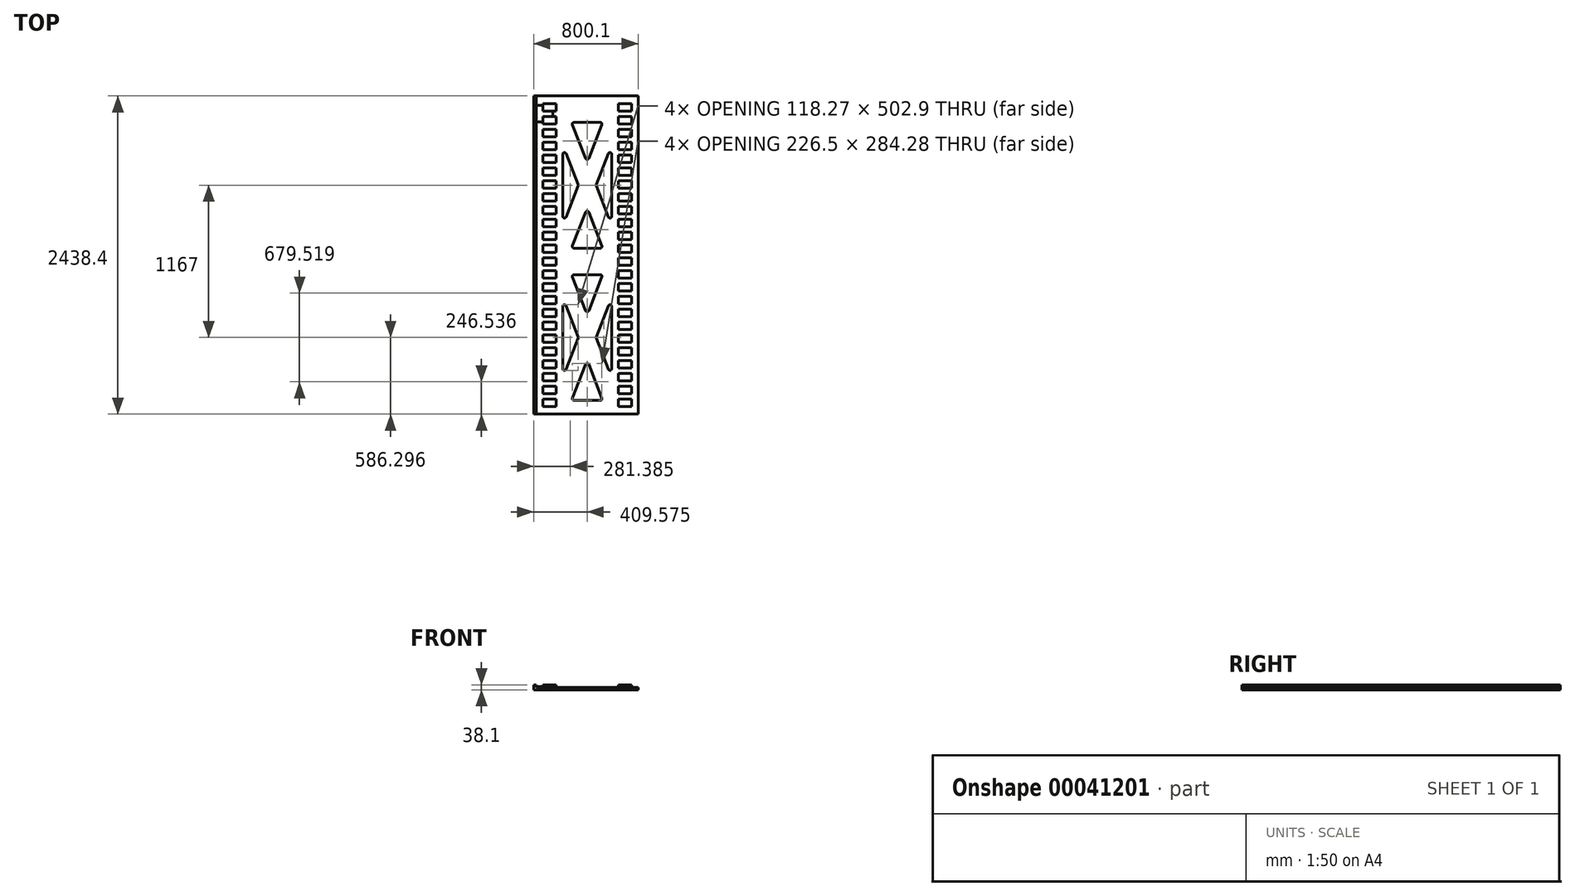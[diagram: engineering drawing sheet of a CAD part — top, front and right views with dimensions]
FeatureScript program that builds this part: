
annotation { "Feature Type Name" : "Feature", "Feature Type Description" : "" }
export const myFeature = defineFeature(function(context is Context, id is Id, definition is map)
    precondition{}
    {
        {
            var Q0;
            Q0=qCreatedBy(makeId("Front.planeOp"),FACE);
            var sketch = newSketch(context, id + "F0", { "sketchPlane" : qUnion([Q0])});
            skLineSegment(sketch, "E0.bottom", {"start": v(0, 0) * mm, "end": v(781.05, 0) * mm});
            skLineSegment(sketch, "E0.top", {"start": v(0, 19.05) * mm, "end": v(781.05, 19.05) * mm});
            skLineSegment(sketch, "E0.left", {"start": v(0, 0) * mm, "end": v(0, 19.05) * mm});
            skLineSegment(sketch, "E0.right", {"start": v(781.05, 0) * mm, "end": v(781.05, 19.05) * mm});
            skSolve(sketch);
        }
        {
            var Q0;
            Q0 = qSketchRegion(id + "F0", true);
            extrude(context, id + "F1", {"entities" : qUnion([Q0]), "depth" : 2438.4 * mm});
        }
        {
            var Q0;
            Q0=makeQuery(id+"F1.opExtrude","SWEPT_FACE",FACE,{"disambiguationData":[OSD([sQuery(id+"F0.wireOp",EDGE,"E0.top")])]});
            var sketch = newSketch(context, id + "F2", { "sketchPlane" : qUnion([Q0])});
            skLineSegment(sketch, "E1.top", {"start": v(50.8, -60.96) * mm, "end": v(152.4, -60.96) * mm});
            skLineSegment(sketch, "E2.top", {"start": v(50.8, -116.71) * mm, "end": v(152.4, -116.71) * mm});
            skLineSegment(sketch, "E2.left", {"start": v(50.8, -60.96) * mm, "end": v(50.8, -116.71) * mm});
            skLineSegment(sketch, "E3", {"start": v(152.4, -60.96) * mm, "end": v(152.4, -116.71) * mm});
            skLineSegment(sketch, "E4.0.1.0", {"start": v(50.8, -159.38) * mm, "end": v(152.4, -159.38) * mm});
            skLineSegment(sketch, "E4.0.1.1", {"start": v(50.8, -215.14) * mm, "end": v(152.4, -215.14) * mm});
            skLineSegment(sketch, "E4.0.1.2", {"start": v(50.8, -159.38) * mm, "end": v(50.8, -215.14) * mm});
            skLineSegment(sketch, "E4.0.1.3", {"start": v(152.4, -159.39) * mm, "end": v(152.4, -215.14) * mm});
            skLineSegment(sketch, "E4.0.2.0", {"start": v(50.8, -257.81) * mm, "end": v(152.4, -257.81) * mm});
            skLineSegment(sketch, "E4.0.2.1", {"start": v(50.8, -313.56) * mm, "end": v(152.4, -313.56) * mm});
            skLineSegment(sketch, "E4.0.2.2", {"start": v(50.8, -257.81) * mm, "end": v(50.8, -313.56) * mm});
            skLineSegment(sketch, "E4.0.2.3", {"start": v(152.4, -257.8) * mm, "end": v(152.4, -313.56) * mm});
            skLineSegment(sketch, "E4.0.3.0", {"start": v(50.8, -356.24) * mm, "end": v(152.4, -356.24) * mm});
            skLineSegment(sketch, "E4.0.3.1", {"start": v(50.8, -411.99) * mm, "end": v(152.4, -411.99) * mm});
            skLineSegment(sketch, "E4.0.3.2", {"start": v(50.8, -356.24) * mm, "end": v(50.8, -411.99) * mm});
            skLineSegment(sketch, "E4.0.3.3", {"start": v(152.4, -356.24) * mm, "end": v(152.4, -411.99) * mm});
            skLineSegment(sketch, "E4.0.4.0", {"start": v(50.8, -454.66) * mm, "end": v(152.4, -454.66) * mm});
            skLineSegment(sketch, "E4.0.4.1", {"start": v(50.8, -510.41) * mm, "end": v(152.4, -510.41) * mm});
            skLineSegment(sketch, "E4.0.4.2", {"start": v(50.8, -454.66) * mm, "end": v(50.8, -510.41) * mm});
            skLineSegment(sketch, "E4.0.4.3", {"start": v(152.4, -454.66) * mm, "end": v(152.4, -510.41) * mm});
            skLineSegment(sketch, "E4.0.5.0", {"start": v(50.8, -553.09) * mm, "end": v(152.4, -553.09) * mm});
            skLineSegment(sketch, "E4.0.5.1", {"start": v(50.8, -608.84) * mm, "end": v(152.4, -608.84) * mm});
            skLineSegment(sketch, "E4.0.5.2", {"start": v(50.8, -553.09) * mm, "end": v(50.8, -608.84) * mm});
            skLineSegment(sketch, "E4.0.5.3", {"start": v(152.4, -553.09) * mm, "end": v(152.4, -608.84) * mm});
            skLineSegment(sketch, "E4.0.6.0", {"start": v(50.8, -651.51) * mm, "end": v(152.4, -651.51) * mm});
            skLineSegment(sketch, "E4.0.6.1", {"start": v(50.8, -707.26) * mm, "end": v(152.4, -707.26) * mm});
            skLineSegment(sketch, "E4.0.6.2", {"start": v(50.8, -651.5) * mm, "end": v(50.8, -707.26) * mm});
            skLineSegment(sketch, "E4.0.6.3", {"start": v(152.4, -651.51) * mm, "end": v(152.4, -707.26) * mm});
            skLineSegment(sketch, "E4.0.7.0", {"start": v(50.8, -749.94) * mm, "end": v(152.4, -749.94) * mm});
            skLineSegment(sketch, "E4.0.7.1", {"start": v(50.8, -805.69) * mm, "end": v(152.4, -805.69) * mm});
            skLineSegment(sketch, "E4.0.7.2", {"start": v(50.8, -749.94) * mm, "end": v(50.8, -805.69) * mm});
            skLineSegment(sketch, "E4.0.7.3", {"start": v(152.4, -749.94) * mm, "end": v(152.4, -805.69) * mm});
            skLineSegment(sketch, "E4.0.8.0", {"start": v(50.8, -848.36) * mm, "end": v(152.4, -848.36) * mm});
            skLineSegment(sketch, "E4.0.8.1", {"start": v(50.8, -904.11) * mm, "end": v(152.4, -904.11) * mm});
            skLineSegment(sketch, "E4.0.8.2", {"start": v(50.8, -848.36) * mm, "end": v(50.8, -904.11) * mm});
            skLineSegment(sketch, "E4.0.8.3", {"start": v(152.4, -848.36) * mm, "end": v(152.4, -904.11) * mm});
            skLineSegment(sketch, "E4.0.9.0", {"start": v(50.8, -946.79) * mm, "end": v(152.4, -946.79) * mm});
            skLineSegment(sketch, "E4.0.9.1", {"start": v(50.8, -1002.54) * mm, "end": v(152.4, -1002.54) * mm});
            skLineSegment(sketch, "E4.0.9.2", {"start": v(50.8, -946.78) * mm, "end": v(50.8, -1002.54) * mm});
            skLineSegment(sketch, "E4.0.9.3", {"start": v(152.4, -946.79) * mm, "end": v(152.4, -1002.54) * mm});
            skLineSegment(sketch, "E4.0.10.0", {"start": v(50.8, -1045.2) * mm, "end": v(152.4, -1045.2) * mm});
            skLineSegment(sketch, "E4.0.10.1", {"start": v(50.8, -1100.96) * mm, "end": v(152.4, -1100.96) * mm});
            skLineSegment(sketch, "E4.0.10.2", {"start": v(50.8, -1045.2) * mm, "end": v(50.8, -1100.96) * mm});
            skLineSegment(sketch, "E4.0.10.3", {"start": v(152.4, -1045.2) * mm, "end": v(152.4, -1100.96) * mm});
            skLineSegment(sketch, "E4.0.11.0", {"start": v(50.8, -1143.63) * mm, "end": v(152.4, -1143.63) * mm});
            skLineSegment(sketch, "E4.0.11.1", {"start": v(50.8, -1199.39) * mm, "end": v(152.4, -1199.39) * mm});
            skLineSegment(sketch, "E4.0.11.2", {"start": v(50.8, -1143.63) * mm, "end": v(50.8, -1199.39) * mm});
            skLineSegment(sketch, "E4.0.11.3", {"start": v(152.4, -1143.63) * mm, "end": v(152.4, -1199.39) * mm});
            skLineSegment(sketch, "E4.0.12.0", {"start": v(50.8, -1242.06) * mm, "end": v(152.4, -1242.06) * mm});
            skLineSegment(sketch, "E4.0.12.1", {"start": v(50.8, -1297.81) * mm, "end": v(152.4, -1297.81) * mm});
            skLineSegment(sketch, "E4.0.12.2", {"start": v(50.8, -1242.06) * mm, "end": v(50.8, -1297.81) * mm});
            skLineSegment(sketch, "E4.0.12.3", {"start": v(152.4, -1242.06) * mm, "end": v(152.4, -1297.81) * mm});
            skLineSegment(sketch, "E4.0.13.0", {"start": v(50.8, -1340.49) * mm, "end": v(152.4, -1340.49) * mm});
            skLineSegment(sketch, "E4.0.13.1", {"start": v(50.8, -1396.24) * mm, "end": v(152.4, -1396.24) * mm});
            skLineSegment(sketch, "E4.0.13.2", {"start": v(50.8, -1340.49) * mm, "end": v(50.8, -1396.24) * mm});
            skLineSegment(sketch, "E4.0.13.3", {"start": v(152.4, -1340.49) * mm, "end": v(152.4, -1396.24) * mm});
            skLineSegment(sketch, "E4.0.14.0", {"start": v(50.8, -1438.9) * mm, "end": v(152.4, -1438.9) * mm});
            skLineSegment(sketch, "E4.0.14.1", {"start": v(50.8, -1494.66) * mm, "end": v(152.4, -1494.66) * mm});
            skLineSegment(sketch, "E4.0.14.2", {"start": v(50.8, -1438.9) * mm, "end": v(50.8, -1494.66) * mm});
            skLineSegment(sketch, "E4.0.14.3", {"start": v(152.4, -1438.9) * mm, "end": v(152.4, -1494.66) * mm});
            skLineSegment(sketch, "E4.0.15.0", {"start": v(50.8, -1537.34) * mm, "end": v(152.4, -1537.34) * mm});
            skLineSegment(sketch, "E4.0.15.1", {"start": v(50.8, -1593.09) * mm, "end": v(152.4, -1593.09) * mm});
            skLineSegment(sketch, "E4.0.15.2", {"start": v(50.8, -1537.34) * mm, "end": v(50.8, -1593.09) * mm});
            skLineSegment(sketch, "E4.0.15.3", {"start": v(152.4, -1537.34) * mm, "end": v(152.4, -1593.09) * mm});
            skLineSegment(sketch, "E4.0.16.0", {"start": v(50.8, -1635.76) * mm, "end": v(152.4, -1635.76) * mm});
            skLineSegment(sketch, "E4.0.16.1", {"start": v(50.8, -1691.51) * mm, "end": v(152.4, -1691.51) * mm});
            skLineSegment(sketch, "E4.0.16.2", {"start": v(50.8, -1635.76) * mm, "end": v(50.8, -1691.51) * mm});
            skLineSegment(sketch, "E4.0.16.3", {"start": v(152.4, -1635.76) * mm, "end": v(152.4, -1691.51) * mm});
            skLineSegment(sketch, "E4.0.17.0", {"start": v(50.8, -1734.19) * mm, "end": v(152.4, -1734.19) * mm});
            skLineSegment(sketch, "E4.0.17.1", {"start": v(50.8, -1789.94) * mm, "end": v(152.4, -1789.94) * mm});
            skLineSegment(sketch, "E4.0.17.2", {"start": v(50.8, -1734.19) * mm, "end": v(50.8, -1789.94) * mm});
            skLineSegment(sketch, "E4.0.17.3", {"start": v(152.4, -1734.19) * mm, "end": v(152.4, -1789.94) * mm});
            skLineSegment(sketch, "E4.0.18.0", {"start": v(50.8, -1832.61) * mm, "end": v(152.4, -1832.61) * mm});
            skLineSegment(sketch, "E4.0.18.1", {"start": v(50.8, -1888.36) * mm, "end": v(152.4, -1888.36) * mm});
            skLineSegment(sketch, "E4.0.18.2", {"start": v(50.8, -1832.61) * mm, "end": v(50.8, -1888.36) * mm});
            skLineSegment(sketch, "E4.0.18.3", {"start": v(152.4, -1832.61) * mm, "end": v(152.4, -1888.36) * mm});
            skLineSegment(sketch, "E4.0.19.0", {"start": v(50.8, -1931.04) * mm, "end": v(152.4, -1931.04) * mm});
            skLineSegment(sketch, "E4.0.19.1", {"start": v(50.8, -1986.79) * mm, "end": v(152.4, -1986.79) * mm});
            skLineSegment(sketch, "E4.0.19.2", {"start": v(50.8, -1931.04) * mm, "end": v(50.8, -1986.79) * mm});
            skLineSegment(sketch, "E4.0.19.3", {"start": v(152.4, -1931.04) * mm, "end": v(152.4, -1986.79) * mm});
            skLineSegment(sketch, "E4.0.20.0", {"start": v(50.8, -2029.46) * mm, "end": v(152.4, -2029.46) * mm});
            skLineSegment(sketch, "E4.0.20.1", {"start": v(50.8, -2085.21) * mm, "end": v(152.4, -2085.21) * mm});
            skLineSegment(sketch, "E4.0.20.2", {"start": v(50.8, -2029.46) * mm, "end": v(50.8, -2085.21) * mm});
            skLineSegment(sketch, "E4.0.20.3", {"start": v(152.4, -2029.46) * mm, "end": v(152.4, -2085.21) * mm});
            skLineSegment(sketch, "E4.0.21.0", {"start": v(50.8, -2127.89) * mm, "end": v(152.4, -2127.89) * mm});
            skLineSegment(sketch, "E4.0.21.1", {"start": v(50.8, -2183.64) * mm, "end": v(152.4, -2183.64) * mm});
            skLineSegment(sketch, "E4.0.21.2", {"start": v(50.8, -2127.89) * mm, "end": v(50.8, -2183.64) * mm});
            skLineSegment(sketch, "E4.0.21.3", {"start": v(152.4, -2127.89) * mm, "end": v(152.4, -2183.64) * mm});
            skLineSegment(sketch, "E4.0.22.0", {"start": v(50.8, -2226.31) * mm, "end": v(152.4, -2226.31) * mm});
            skLineSegment(sketch, "E4.0.22.1", {"start": v(50.8, -2282.06) * mm, "end": v(152.4, -2282.06) * mm});
            skLineSegment(sketch, "E4.0.22.2", {"start": v(50.8, -2226.31) * mm, "end": v(50.8, -2282.06) * mm});
            skLineSegment(sketch, "E4.0.22.3", {"start": v(152.4, -2226.31) * mm, "end": v(152.4, -2282.06) * mm});
            skLineSegment(sketch, "E4.0.23.0", {"start": v(50.8, -2324.74) * mm, "end": v(152.4, -2324.74) * mm});
            skLineSegment(sketch, "E4.0.23.1", {"start": v(50.8, -2380.49) * mm, "end": v(152.4, -2380.49) * mm});
            skLineSegment(sketch, "E4.0.23.2", {"start": v(50.8, -2324.74) * mm, "end": v(50.8, -2380.49) * mm});
            skLineSegment(sketch, "E4.0.23.3", {"start": v(152.4, -2324.74) * mm, "end": v(152.4, -2380.49) * mm});
            skLineSegment(sketch, "E4.1.0.0", {"start": v(628.65, -60.96) * mm, "end": v(730.25, -60.96) * mm});
            skLineSegment(sketch, "E4.1.0.1", {"start": v(628.65, -116.71) * mm, "end": v(730.25, -116.71) * mm});
            skLineSegment(sketch, "E4.1.0.2", {"start": v(628.65, -60.96) * mm, "end": v(628.65, -116.71) * mm});
            skLineSegment(sketch, "E4.1.0.3", {"start": v(730.25, -60.96) * mm, "end": v(730.25, -116.71) * mm});
            skLineSegment(sketch, "E4.1.1.0", {"start": v(628.65, -159.38) * mm, "end": v(730.25, -159.38) * mm});
            skLineSegment(sketch, "E4.1.1.1", {"start": v(628.65, -215.14) * mm, "end": v(730.25, -215.14) * mm});
            skLineSegment(sketch, "E4.1.1.2", {"start": v(628.65, -159.38) * mm, "end": v(628.65, -215.14) * mm});
            skLineSegment(sketch, "E4.1.1.3", {"start": v(730.25, -159.38) * mm, "end": v(730.25, -215.14) * mm});
            skLineSegment(sketch, "E4.1.2.0", {"start": v(628.65, -257.81) * mm, "end": v(730.25, -257.81) * mm});
            skLineSegment(sketch, "E4.1.2.1", {"start": v(628.65, -313.56) * mm, "end": v(730.25, -313.56) * mm});
            skLineSegment(sketch, "E4.1.2.2", {"start": v(628.65, -257.8) * mm, "end": v(628.65, -313.56) * mm});
            skLineSegment(sketch, "E4.1.2.3", {"start": v(730.25, -257.81) * mm, "end": v(730.25, -313.56) * mm});
            skLineSegment(sketch, "E4.1.3.0", {"start": v(628.65, -356.24) * mm, "end": v(730.25, -356.24) * mm});
            skLineSegment(sketch, "E4.1.3.1", {"start": v(628.65, -411.99) * mm, "end": v(730.25, -411.99) * mm});
            skLineSegment(sketch, "E4.1.3.2", {"start": v(628.65, -356.24) * mm, "end": v(628.65, -411.99) * mm});
            skLineSegment(sketch, "E4.1.3.3", {"start": v(730.25, -356.24) * mm, "end": v(730.25, -411.99) * mm});
            skLineSegment(sketch, "E4.1.4.0", {"start": v(628.65, -454.66) * mm, "end": v(730.25, -454.66) * mm});
            skLineSegment(sketch, "E4.1.4.1", {"start": v(628.65, -510.41) * mm, "end": v(730.25, -510.41) * mm});
            skLineSegment(sketch, "E4.1.4.2", {"start": v(628.65, -454.66) * mm, "end": v(628.65, -510.41) * mm});
            skLineSegment(sketch, "E4.1.4.3", {"start": v(730.25, -454.66) * mm, "end": v(730.25, -510.41) * mm});
            skLineSegment(sketch, "E4.1.5.0", {"start": v(628.65, -553.09) * mm, "end": v(730.25, -553.09) * mm});
            skLineSegment(sketch, "E4.1.5.1", {"start": v(628.65, -608.84) * mm, "end": v(730.25, -608.84) * mm});
            skLineSegment(sketch, "E4.1.5.2", {"start": v(628.65, -553.09) * mm, "end": v(628.65, -608.84) * mm});
            skLineSegment(sketch, "E4.1.5.3", {"start": v(730.25, -553.09) * mm, "end": v(730.25, -608.84) * mm});
            skLineSegment(sketch, "E4.1.6.0", {"start": v(628.65, -651.51) * mm, "end": v(730.25, -651.51) * mm});
            skLineSegment(sketch, "E4.1.6.1", {"start": v(628.65, -707.26) * mm, "end": v(730.25, -707.26) * mm});
            skLineSegment(sketch, "E4.1.6.2", {"start": v(628.65, -651.51) * mm, "end": v(628.65, -707.26) * mm});
            skLineSegment(sketch, "E4.1.6.3", {"start": v(730.25, -651.51) * mm, "end": v(730.25, -707.26) * mm});
            skLineSegment(sketch, "E4.1.7.0", {"start": v(628.65, -749.94) * mm, "end": v(730.25, -749.94) * mm});
            skLineSegment(sketch, "E4.1.7.1", {"start": v(628.65, -805.69) * mm, "end": v(730.25, -805.69) * mm});
            skLineSegment(sketch, "E4.1.7.2", {"start": v(628.65, -749.94) * mm, "end": v(628.65, -805.69) * mm});
            skLineSegment(sketch, "E4.1.7.3", {"start": v(730.25, -749.94) * mm, "end": v(730.25, -805.69) * mm});
            skLineSegment(sketch, "E4.1.8.0", {"start": v(628.65, -848.36) * mm, "end": v(730.25, -848.36) * mm});
            skLineSegment(sketch, "E4.1.8.1", {"start": v(628.65, -904.11) * mm, "end": v(730.25, -904.11) * mm});
            skLineSegment(sketch, "E4.1.8.2", {"start": v(628.65, -848.36) * mm, "end": v(628.65, -904.11) * mm});
            skLineSegment(sketch, "E4.1.8.3", {"start": v(730.25, -848.36) * mm, "end": v(730.25, -904.11) * mm});
            skLineSegment(sketch, "E4.1.9.0", {"start": v(628.65, -946.79) * mm, "end": v(730.25, -946.79) * mm});
            skLineSegment(sketch, "E4.1.9.1", {"start": v(628.65, -1002.54) * mm, "end": v(730.25, -1002.54) * mm});
            skLineSegment(sketch, "E4.1.9.2", {"start": v(628.65, -946.79) * mm, "end": v(628.65, -1002.54) * mm});
            skLineSegment(sketch, "E4.1.9.3", {"start": v(730.25, -946.79) * mm, "end": v(730.25, -1002.54) * mm});
            skLineSegment(sketch, "E4.1.10.0", {"start": v(628.65, -1045.2) * mm, "end": v(730.25, -1045.2) * mm});
            skLineSegment(sketch, "E4.1.10.1", {"start": v(628.65, -1100.96) * mm, "end": v(730.25, -1100.96) * mm});
            skLineSegment(sketch, "E4.1.10.2", {"start": v(628.65, -1045.2) * mm, "end": v(628.65, -1100.96) * mm});
            skLineSegment(sketch, "E4.1.10.3", {"start": v(730.25, -1045.2) * mm, "end": v(730.25, -1100.96) * mm});
            skLineSegment(sketch, "E4.1.11.0", {"start": v(628.65, -1143.63) * mm, "end": v(730.25, -1143.63) * mm});
            skLineSegment(sketch, "E4.1.11.1", {"start": v(628.65, -1199.39) * mm, "end": v(730.25, -1199.39) * mm});
            skLineSegment(sketch, "E4.1.11.2", {"start": v(628.65, -1143.63) * mm, "end": v(628.65, -1199.39) * mm});
            skLineSegment(sketch, "E4.1.11.3", {"start": v(730.25, -1143.63) * mm, "end": v(730.25, -1199.39) * mm});
            skLineSegment(sketch, "E4.1.12.0", {"start": v(628.65, -1242.06) * mm, "end": v(730.25, -1242.06) * mm});
            skLineSegment(sketch, "E4.1.12.1", {"start": v(628.65, -1297.81) * mm, "end": v(730.25, -1297.81) * mm});
            skLineSegment(sketch, "E4.1.12.2", {"start": v(628.65, -1242.06) * mm, "end": v(628.65, -1297.81) * mm});
            skLineSegment(sketch, "E4.1.12.3", {"start": v(730.25, -1242.06) * mm, "end": v(730.25, -1297.81) * mm});
            skLineSegment(sketch, "E4.1.13.0", {"start": v(628.65, -1340.49) * mm, "end": v(730.25, -1340.49) * mm});
            skLineSegment(sketch, "E4.1.13.1", {"start": v(628.65, -1396.24) * mm, "end": v(730.25, -1396.24) * mm});
            skLineSegment(sketch, "E4.1.13.2", {"start": v(628.65, -1340.49) * mm, "end": v(628.65, -1396.24) * mm});
            skLineSegment(sketch, "E4.1.13.3", {"start": v(730.25, -1340.49) * mm, "end": v(730.25, -1396.24) * mm});
            skLineSegment(sketch, "E4.1.14.0", {"start": v(628.65, -1438.9) * mm, "end": v(730.25, -1438.9) * mm});
            skLineSegment(sketch, "E4.1.14.1", {"start": v(628.65, -1494.66) * mm, "end": v(730.25, -1494.66) * mm});
            skLineSegment(sketch, "E4.1.14.2", {"start": v(628.65, -1438.9) * mm, "end": v(628.65, -1494.66) * mm});
            skLineSegment(sketch, "E4.1.14.3", {"start": v(730.25, -1438.9) * mm, "end": v(730.25, -1494.66) * mm});
            skLineSegment(sketch, "E4.1.15.0", {"start": v(628.65, -1537.34) * mm, "end": v(730.25, -1537.34) * mm});
            skLineSegment(sketch, "E4.1.15.1", {"start": v(628.65, -1593.09) * mm, "end": v(730.25, -1593.09) * mm});
            skLineSegment(sketch, "E4.1.15.2", {"start": v(628.65, -1537.34) * mm, "end": v(628.65, -1593.09) * mm});
            skLineSegment(sketch, "E4.1.15.3", {"start": v(730.25, -1537.34) * mm, "end": v(730.25, -1593.09) * mm});
            skLineSegment(sketch, "E4.1.16.0", {"start": v(628.65, -1635.76) * mm, "end": v(730.25, -1635.76) * mm});
            skLineSegment(sketch, "E4.1.16.1", {"start": v(628.65, -1691.51) * mm, "end": v(730.25, -1691.51) * mm});
            skLineSegment(sketch, "E4.1.16.2", {"start": v(628.65, -1635.76) * mm, "end": v(628.65, -1691.51) * mm});
            skLineSegment(sketch, "E4.1.16.3", {"start": v(730.25, -1635.76) * mm, "end": v(730.25, -1691.51) * mm});
            skLineSegment(sketch, "E4.1.17.0", {"start": v(628.65, -1734.19) * mm, "end": v(730.25, -1734.19) * mm});
            skLineSegment(sketch, "E4.1.17.1", {"start": v(628.65, -1789.94) * mm, "end": v(730.25, -1789.94) * mm});
            skLineSegment(sketch, "E4.1.17.2", {"start": v(628.65, -1734.19) * mm, "end": v(628.65, -1789.94) * mm});
            skLineSegment(sketch, "E4.1.17.3", {"start": v(730.25, -1734.19) * mm, "end": v(730.25, -1789.94) * mm});
            skLineSegment(sketch, "E4.1.18.0", {"start": v(628.65, -1832.61) * mm, "end": v(730.25, -1832.61) * mm});
            skLineSegment(sketch, "E4.1.18.1", {"start": v(628.65, -1888.36) * mm, "end": v(730.25, -1888.36) * mm});
            skLineSegment(sketch, "E4.1.18.2", {"start": v(628.65, -1832.61) * mm, "end": v(628.65, -1888.36) * mm});
            skLineSegment(sketch, "E4.1.18.3", {"start": v(730.25, -1832.61) * mm, "end": v(730.25, -1888.36) * mm});
            skLineSegment(sketch, "E4.1.19.0", {"start": v(628.65, -1931.04) * mm, "end": v(730.25, -1931.04) * mm});
            skLineSegment(sketch, "E4.1.19.1", {"start": v(628.65, -1986.79) * mm, "end": v(730.25, -1986.79) * mm});
            skLineSegment(sketch, "E4.1.19.2", {"start": v(628.65, -1931.04) * mm, "end": v(628.65, -1986.79) * mm});
            skLineSegment(sketch, "E4.1.19.3", {"start": v(730.25, -1931.04) * mm, "end": v(730.25, -1986.79) * mm});
            skLineSegment(sketch, "E4.1.20.0", {"start": v(628.65, -2029.46) * mm, "end": v(730.25, -2029.46) * mm});
            skLineSegment(sketch, "E4.1.20.1", {"start": v(628.65, -2085.21) * mm, "end": v(730.25, -2085.21) * mm});
            skLineSegment(sketch, "E4.1.20.2", {"start": v(628.65, -2029.46) * mm, "end": v(628.65, -2085.21) * mm});
            skLineSegment(sketch, "E4.1.20.3", {"start": v(730.25, -2029.46) * mm, "end": v(730.25, -2085.21) * mm});
            skLineSegment(sketch, "E4.1.21.0", {"start": v(628.65, -2127.89) * mm, "end": v(730.25, -2127.89) * mm});
            skLineSegment(sketch, "E4.1.21.1", {"start": v(628.65, -2183.64) * mm, "end": v(730.25, -2183.64) * mm});
            skLineSegment(sketch, "E4.1.21.2", {"start": v(628.65, -2127.89) * mm, "end": v(628.65, -2183.64) * mm});
            skLineSegment(sketch, "E4.1.21.3", {"start": v(730.25, -2127.89) * mm, "end": v(730.25, -2183.64) * mm});
            skLineSegment(sketch, "E4.1.22.0", {"start": v(628.65, -2226.31) * mm, "end": v(730.25, -2226.31) * mm});
            skLineSegment(sketch, "E4.1.22.1", {"start": v(628.65, -2282.06) * mm, "end": v(730.25, -2282.06) * mm});
            skLineSegment(sketch, "E4.1.22.2", {"start": v(628.65, -2226.31) * mm, "end": v(628.65, -2282.06) * mm});
            skLineSegment(sketch, "E4.1.22.3", {"start": v(730.25, -2226.31) * mm, "end": v(730.25, -2282.06) * mm});
            skLineSegment(sketch, "E4.1.23.0", {"start": v(628.65, -2324.74) * mm, "end": v(730.25, -2324.74) * mm});
            skLineSegment(sketch, "E4.1.23.1", {"start": v(628.65, -2380.49) * mm, "end": v(730.25, -2380.49) * mm});
            skLineSegment(sketch, "E4.1.23.2", {"start": v(628.65, -2324.74) * mm, "end": v(628.65, -2380.49) * mm});
            skLineSegment(sketch, "E4.1.23.3", {"start": v(730.25, -2324.74) * mm, "end": v(730.25, -2380.49) * mm});
            skLineSegment(sketch, "E4.direction1", {"start": v(50.8, -116.71) * mm, "end": v(628.65, -116.71) * mm, "construction": true});
            skLineSegment(sketch, "E4.direction2", {"start": v(50.8, -116.71) * mm, "end": v(50.8, -215.14) * mm, "construction": true});
            skSolve(sketch);
        }
        {
            var Q0;
            Q0 = qSketchRegion(id + "F2", true);
            extrude(context, id + "F3", {"entities" : qUnion([Q0]), "depth" : 19.05 * mm});
        }
        {
            var Q0;
            Q0=makeQuery(id+"F1.opExtrude","CAP_FACE",FACE,{"disambiguationData":[OSD([sQuery(id+"F0.wireOp",EDGE,"E0.bottom"),sQuery(id+"F0.wireOp",EDGE,"E0.top"),sQuery(id+"F0.wireOp",EDGE,"E0.left"),sQuery(id+"F0.wireOp",EDGE,"E0.right")])],"isStart":true});
            var sketch = newSketch(context, id + "F4", { "sketchPlane" : qUnion([Q0])});
            skLineSegment(sketch, "E5.bottom", {"start": v(0, 0) * mm, "end": v(19.05, 0) * mm});
            skLineSegment(sketch, "E5.top", {"start": v(0, 38.1) * mm, "end": v(19.05, 38.1) * mm});
            skLineSegment(sketch, "E5.left", {"start": v(0, 0) * mm, "end": v(0, 38.1) * mm});
            skLineSegment(sketch, "E5.right", {"start": v(19.05, 0) * mm, "end": v(19.05, 38.1) * mm});
            skSolve(sketch);
        }
        {
            var Q0;
            Q0 = qSketchRegion(id + "F4", true);
            extrude(context, id + "F5", {"entities" : qUnion([Q0]), "operationType" : NewBodyOperationType.ADD, "oppositeDirection" : true, "depth" : 2438.4 * mm});
        }
        {
            var Q0;
            Q0=makeQuery(id+"F1.opExtrude","SWEPT_FACE",FACE,{"disambiguationData":[OSD([sQuery(id+"F0.wireOp",EDGE,"E0.top")])]});
            var sketch = newSketch(context, id + "F6", { "sketchPlane" : qUnion([Q0])});
            skLineSegment(sketch, "E6.0", {"start": v(289.9, -203.2) * mm, "end": v(491.16, -203.2) * mm});
            skLineSegment(sketch, "E7", {"start": v(203.2, -924.01) * mm, "end": v(203.2, -446.19) * mm});
            skLineSegment(sketch, "E8", {"start": v(577.85, -924.01) * mm, "end": v(577.85, -446.19) * mm});
            skLineSegment(sketch, "E9", {"start": v(0, -1268.6) * mm, "end": v(929.8, -1268.6) * mm});
            skPoint(sketch, "E9.startSnap0", {"position": v(50.8, -1268.6) * mm});
            skPoint(sketch, "E9.endSnap0", {"position": v(752.48, -1268.6) * mm});
            skLineSegment(sketch, "E10.0", {"start": v(289.9, -1167) * mm, "end": v(491.16, -1167) * mm});
            skLineSegment(sketch, "E11.0", {"start": v(503, -220.5) * mm, "end": v(402.36, -479.39) * mm});
            skLineSegment(sketch, "E12.0", {"start": v(553.31, -441.59) * mm, "end": v(460.44, -680.5) * mm});
            skLineSegment(sketch, "E13.0", {"start": v(227.74, -441.59) * mm, "end": v(320.6, -680.5) * mm});
            skLineSegment(sketch, "E14.0", {"start": v(278.05, -220.5) * mm, "end": v(378.69, -479.39) * mm});
            skLineSegment(sketch, "E15", {"start": v(320.6, -689.7) * mm, "end": v(227.74, -928.62) * mm});
            skLineSegment(sketch, "E16", {"start": v(402.36, -890.82) * mm, "end": v(503, -1149.7) * mm});
            skLineSegment(sketch, "E17", {"start": v(378.69, -890.82) * mm, "end": v(278.05, -1149.7) * mm});
            skLineSegment(sketch, "E18", {"start": v(460.44, -689.7) * mm, "end": v(553.31, -928.62) * mm});
            skArc(sketch, "E19.filletArc", {"start": v(577.85, -446.19) * mm, "mid": v(567.5, -433.7) * mm, "end": v(553.31, -441.59) * mm});
            skArc(sketch, "E20.filletArc", {"start": v(460.44, -680.5) * mm, "mid": v(459.58, -685.1) * mm, "end": v(460.44, -689.7) * mm});
            skArc(sketch, "E21.filletArc", {"start": v(553.31, -928.62) * mm, "mid": v(567.5, -936.5) * mm, "end": v(577.85, -924.01) * mm});
            skArc(sketch, "E22.filletArc", {"start": v(402.36, -890.82) * mm, "mid": v(390.52, -882.72) * mm, "end": v(378.69, -890.82) * mm});
            skArc(sketch, "E23.filletArc", {"start": v(278.05, -1149.7) * mm, "mid": v(279.4, -1161.47) * mm, "end": v(289.9, -1167) * mm});
            skArc(sketch, "E24.filletArc", {"start": v(491.16, -1167) * mm, "mid": v(501.64, -1161.47) * mm, "end": v(503, -1149.7) * mm});
            skArc(sketch, "E25.filletArc", {"start": v(203.2, -924.01) * mm, "mid": v(213.56, -936.5) * mm, "end": v(227.74, -928.62) * mm});
            skArc(sketch, "E26.filletArc", {"start": v(320.6, -689.7) * mm, "mid": v(321.47, -685.1) * mm, "end": v(320.6, -680.5) * mm});
            skArc(sketch, "E27.filletArc", {"start": v(227.74, -441.59) * mm, "mid": v(213.56, -433.7) * mm, "end": v(203.2, -446.19) * mm});
            skArc(sketch, "E28.filletArc", {"start": v(378.69, -479.39) * mm, "mid": v(390.52, -487.48) * mm, "end": v(402.36, -479.39) * mm});
            skArc(sketch, "E29.filletArc", {"start": v(503, -220.5) * mm, "mid": v(501.64, -208.73) * mm, "end": v(491.16, -203.2) * mm});
            skArc(sketch, "E30.filletArc", {"start": v(289.9, -203.2) * mm, "mid": v(279.4, -208.73) * mm, "end": v(278.05, -220.5) * mm});
            skArc(sketch, "E31.MirrorCS", {"start": v(402.36, -1646.39) * mm, "mid": v(390.52, -1654.49) * mm, "end": v(378.69, -1646.39) * mm});
            skArc(sketch, "E32.MirrorCS", {"start": v(320.6, -1847.5) * mm, "mid": v(321.47, -1852.1) * mm, "end": v(320.6, -1856.7) * mm});
            skArc(sketch, "E33.MirrorCS", {"start": v(553.31, -1608.6) * mm, "mid": v(567.5, -1600.7) * mm, "end": v(577.85, -1613.2) * mm});
            skArc(sketch, "E34.MirrorCS", {"start": v(460.44, -1856.7) * mm, "mid": v(459.58, -1852.1) * mm, "end": v(460.44, -1847.5) * mm});
            skArc(sketch, "E35.MirrorCS", {"start": v(378.69, -2057.82) * mm, "mid": v(390.52, -2049.72) * mm, "end": v(402.36, -2057.82) * mm});
            skArc(sketch, "E36.MirrorCS", {"start": v(577.85, -2091.02) * mm, "mid": v(567.5, -2103.5) * mm, "end": v(553.31, -2095.62) * mm});
            skArc(sketch, "E37.MirrorCS", {"start": v(278.05, -1387.5) * mm, "mid": v(279.4, -1375.73) * mm, "end": v(289.9, -1370.2) * mm});
            skArc(sketch, "E38.MirrorCS", {"start": v(503, -2316.7) * mm, "mid": v(501.64, -2328.48) * mm, "end": v(491.16, -2334) * mm});
            skArc(sketch, "E39.MirrorCS", {"start": v(203.2, -1613.2) * mm, "mid": v(213.56, -1600.7) * mm, "end": v(227.74, -1608.6) * mm});
            skArc(sketch, "E40.MirrorCS", {"start": v(289.9, -2334) * mm, "mid": v(279.4, -2328.48) * mm, "end": v(278.05, -2316.7) * mm});
            skArc(sketch, "E41.MirrorCS", {"start": v(491.16, -1370.2) * mm, "mid": v(501.64, -1375.73) * mm, "end": v(503, -1387.5) * mm});
            skArc(sketch, "E42.MirrorCS", {"start": v(227.74, -2095.62) * mm, "mid": v(213.56, -2103.5) * mm, "end": v(203.2, -2091.02) * mm});
            skLineSegment(sketch, "E43.MirrorCS", {"start": v(402.36, -1646.39) * mm, "end": v(503, -1387.5) * mm});
            skLineSegment(sketch, "E44.MirrorCS", {"start": v(378.69, -1646.39) * mm, "end": v(278.05, -1387.5) * mm});
            skLineSegment(sketch, "E45.MirrorCS", {"start": v(503, -2316.7) * mm, "end": v(402.36, -2057.82) * mm});
            skLineSegment(sketch, "E46.MirrorCS", {"start": v(278.05, -2316.7) * mm, "end": v(378.69, -2057.82) * mm});
            skLineSegment(sketch, "E47.MirrorCS", {"start": v(227.74, -2095.62) * mm, "end": v(320.6, -1856.7) * mm});
            skLineSegment(sketch, "E48.MirrorCS", {"start": v(460.44, -1847.5) * mm, "end": v(553.31, -1608.6) * mm});
            skLineSegment(sketch, "E49.MirrorCS", {"start": v(553.31, -2095.62) * mm, "end": v(460.44, -1856.7) * mm});
            skLineSegment(sketch, "E50.MirrorCS", {"start": v(577.85, -1613.2) * mm, "end": v(577.85, -2091.02) * mm});
            skLineSegment(sketch, "E51.MirrorCS", {"start": v(320.6, -1847.5) * mm, "end": v(227.74, -1608.6) * mm});
            skLineSegment(sketch, "E52.MirrorCS", {"start": v(203.2, -1613.2) * mm, "end": v(203.2, -2091.02) * mm});
            skLineSegment(sketch, "E53.MirrorCS", {"start": v(289.9, -2334) * mm, "end": v(491.16, -2334) * mm});
            skLineSegment(sketch, "E54.MirrorCS", {"start": v(289.9, -1370.2) * mm, "end": v(491.16, -1370.2) * mm});
            skSolve(sketch);
        }
        {
            var Q0;
            Q0 = qSketchRegion(id + "F6", true);
            extrude(context, id + "F7", {"entities" : qUnion([Q0]), "operationType" : NewBodyOperationType.REMOVE, "endBound" : BoundingType.UP_TO_NEXT, "oppositeDirection" : true, "depth" : 25.4 * mm});
        }
        {
            var Q0;
            Q0=makeQuery(id+"F1.opExtrude","SWEPT_FACE",FACE,{"disambiguationData":[OSD([sQuery(id+"F0.wireOp",EDGE,"E0.top")])]});
            var sketch = newSketch(context, id + "F8", { "sketchPlane" : qUnion([Q0])});
            skLineSegment(sketch, "E55", {"start": v(0, -73.02) * mm, "end": v(0, -200.03) * mm});
            skLineSegment(sketch, "E56", {"start": v(0, -200.03) * mm, "end": v(50.8, -200.03) * mm});
            skLineSegment(sketch, "E57", {"start": v(50.8, -200.03) * mm, "end": v(50.8, -159.39) * mm});
            skLineSegment(sketch, "E58", {"start": v(50.8, -159.38) * mm, "end": v(127, -159.38) * mm});
            skLineSegment(sketch, "E59", {"start": v(127, -159.39) * mm, "end": v(127, -116.71) * mm});
            skLineSegment(sketch, "E60", {"start": v(127, -116.71) * mm, "end": v(50.8, -116.71) * mm});
            skLineSegment(sketch, "E61", {"start": v(50.8, -116.71) * mm, "end": v(50.8, -73.02) * mm});
            skLineSegment(sketch, "E62", {"start": v(50.8, -73.02) * mm, "end": v(0, -73.02) * mm});
            skSolve(sketch);
        }
        {
            var Q0;
            Q0=makeQuery(id+"F8.imprint","IMPRINT",FACE,{"disambiguationData":[TD([[makeQuery(id+"F8.imprint","IMPRINT",EDGE,{"derivedFrom":sQuery(id+"F8.wireOp",EDGE,"E55")}),-1.0]])]});
            extrude(context, id + "F9", {"entities" : qUnion([Q0]), "depth" : 6.35 * mm});
        }
    });
